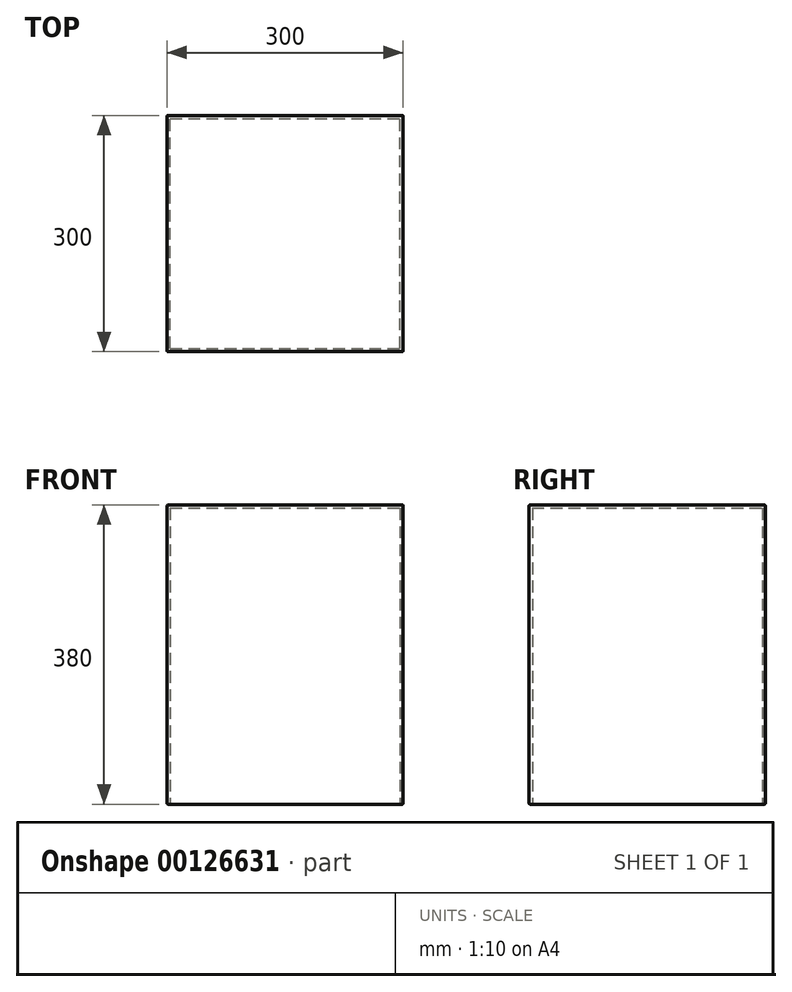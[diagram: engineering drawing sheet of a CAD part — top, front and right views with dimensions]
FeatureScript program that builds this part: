
annotation { "Feature Type Name" : "Feature", "Feature Type Description" : "" }
export const myFeature = defineFeature(function(context is Context, id is Id, definition is map)
    precondition{}
    {
        {
            var Q0;
            Q0=qCreatedBy(makeId("Front.planeOp"),FACE);
            var sketch = newSketch(context, id + "F0", { "sketchPlane" : qUnion([Q0])});
            skLineSegment(sketch, "E0.bottom", {"start": v(-252.56, 331.55) * mm, "end": v(47.44, 331.55) * mm});
            skLineSegment(sketch, "E0.top", {"start": v(-252.56, -48.45) * mm, "end": v(-248.56, -48.45) * mm});
            skLineSegment(sketch, "E0.left", {"start": v(-252.56, 331.55) * mm, "end": v(-252.56, -48.45) * mm});
            skLineSegment(sketch, "E0.right", {"start": v(47.44, 331.55) * mm, "end": v(47.44, -48.45) * mm});
            skLineSegment(sketch, "E1.1", {"start": v(-248.56, 327.55) * mm, "end": v(-248.56, -44.45) * mm});
            skLineSegment(sketch, "E1.2", {"start": v(-248.56, 327.55) * mm, "end": v(43.44, 327.55) * mm});
            skLineSegment(sketch, "E1.3", {"start": v(43.44, 327.55) * mm, "end": v(43.44, -44.45) * mm});
            skLineSegment(sketch, "E2", {"start": v(-248.56, -44.45) * mm, "end": v(-248.56, -48.45) * mm});
            skLineSegment(sketch, "E3", {"start": v(43.44, -44.45) * mm, "end": v(43.44, -48.45) * mm});
            skLineSegment(sketch, "E4.trimOffspring", {"start": v(43.44, -48.45) * mm, "end": v(47.44, -48.45) * mm});
            skSolve(sketch);
        }
        {
            var Q0;
            Q0=makeQuery(id+"F0.imprint","IMPRINT",FACE,{"disambiguationData":[TD([[makeQuery(id+"F0.imprint","IMPRINT",EDGE,{"derivedFrom":sQuery(id+"F0.wireOp",EDGE,"E0.bottom")}),-1.0]])]});
            extrude(context, id + "F1", {"entities" : qUnion([Q0]), "depth" : (300 - 8) * mm});
        }
        {
            var Q0;
            Q0=makeQuery(id+"F1.opExtrude","CAP_FACE",FACE,{"disambiguationData":[OSD([sQuery(id+"F0.wireOp",EDGE,"E0.bottom"),sQuery(id+"F0.wireOp",EDGE,"E0.top"),sQuery(id+"F0.wireOp",EDGE,"E0.left"),sQuery(id+"F0.wireOp",EDGE,"E0.right"),sQuery(id+"F0.wireOp",EDGE,"E1.1"),sQuery(id+"F0.wireOp",EDGE,"E1.2"),sQuery(id+"F0.wireOp",EDGE,"E1.3"),sQuery(id+"F0.wireOp",EDGE,"E2"),sQuery(id+"F0.wireOp",EDGE,"E3"),sQuery(id+"F0.wireOp",EDGE,"E4.trimOffspring")])],"isStart":false});
            var sketch = newSketch(context, id + "F2", { "sketchPlane" : qUnion([Q0])});
            skLineSegment(sketch, "E5.bottom", {"start": v(-252.56, 331.55) * mm, "end": v(47.44, 331.55) * mm});
            skLineSegment(sketch, "E5.top", {"start": v(-252.56, -48.45) * mm, "end": v(47.44, -48.45) * mm});
            skLineSegment(sketch, "E5.left", {"start": v(-252.56, 331.55) * mm, "end": v(-252.56, -48.45) * mm});
            skLineSegment(sketch, "E5.right", {"start": v(47.44, 331.55) * mm, "end": v(47.44, -48.45) * mm});
            skSolve(sketch);
        }
        {
            var Q0;
            Q0=makeQuery(id+"F2.imprint","IMPRINT",FACE,{"disambiguationData":[TD([[makeQuery(id+"F2.imprint","IMPRINT",EDGE,{"derivedFrom":makeQuery(id+"F1.opExtrude","CAP_EDGE",EDGE,{"disambiguationData":[OSD([sQuery(id+"F0.wireOp",EDGE,"E1.2")])],"isStart":false})}),-1.0]])]});
            var Q1;
            Q1=makeQuery(id+"F2.imprint","IMPRINT",FACE,{"disambiguationData":[TD([[makeQuery(id+"F2.imprint","IMPRINT",EDGE,{"derivedFrom":sQuery(id+"F2.wireOp",EDGE,"E5.bottom")}),-1.0]])]});
            extrude(context, id + "F3", {"entities" : qUnion([Q0, Q1]), "operationType" : NewBodyOperationType.ADD, "depth" : 4 * mm});
        }
        {
            var Q0;
            Q0=makeQuery(id+"F1.opExtrude","CAP_FACE",FACE,{"disambiguationData":[OSD([sQuery(id+"F0.wireOp",EDGE,"E0.bottom"),sQuery(id+"F0.wireOp",EDGE,"E0.top"),sQuery(id+"F0.wireOp",EDGE,"E0.left"),sQuery(id+"F0.wireOp",EDGE,"E0.right"),sQuery(id+"F0.wireOp",EDGE,"E1.1"),sQuery(id+"F0.wireOp",EDGE,"E1.2"),sQuery(id+"F0.wireOp",EDGE,"E1.3"),sQuery(id+"F0.wireOp",EDGE,"E2"),sQuery(id+"F0.wireOp",EDGE,"E3"),sQuery(id+"F0.wireOp",EDGE,"E4.trimOffspring")])],"isStart":true});
            var sketch = newSketch(context, id + "F4", { "sketchPlane" : qUnion([Q0])});
            skLineSegment(sketch, "E6.bottom", {"start": v(-47.44, 331.55) * mm, "end": v(252.56, 331.55) * mm});
            skLineSegment(sketch, "E6.top", {"start": v(-47.44, -48.45) * mm, "end": v(252.56, -48.45) * mm});
            skLineSegment(sketch, "E6.left", {"start": v(-47.44, 331.55) * mm, "end": v(-47.44, -48.45) * mm});
            skLineSegment(sketch, "E6.right", {"start": v(252.56, 331.55) * mm, "end": v(252.56, -48.45) * mm});
            skSolve(sketch);
        }
        {
            var Q0;
            Q0=makeQuery(id+"F4.imprint","IMPRINT",FACE,{"disambiguationData":[TD([[makeQuery(id+"F4.imprint","IMPRINT",EDGE,{"derivedFrom":sQuery(id+"F4.wireOp",EDGE,"E6.bottom")}),1.0]])]});
            var Q1;
            Q1=makeQuery(id+"F4.imprint","IMPRINT",FACE,{"disambiguationData":[TD([[makeQuery(id+"F4.imprint","IMPRINT",EDGE,{"derivedFrom":makeQuery(id+"F1.opExtrude","CAP_EDGE",EDGE,{"disambiguationData":[OSD([sQuery(id+"F0.wireOp",EDGE,"E1.2")])],"isStart":true})}),1.0]])]});
            extrude(context, id + "F5", {"entities" : qUnion([Q0, Q1]), "operationType" : NewBodyOperationType.ADD, "depth" : 4 * mm});
        }
        {
            var Q0;
            Q0=makeQuery(id+"F5.opExtrude","CAP_FACE",FACE,{"disambiguationData":[OSD([sQuery(id+"F4.wireOp",EDGE,"E6.bottom"),sQuery(id+"F4.wireOp",EDGE,"E6.top"),sQuery(id+"F4.wireOp",EDGE,"E6.left"),sQuery(id+"F4.wireOp",EDGE,"E6.right")])],"isStart":false});
            var Q1;
            Q1=makeQuery(id+"F5.boolean.opBoolean","MERGE",FACE,{"derivedFrom":[makeQuery(id+"F3.boolean.opBoolean","MERGE",FACE,{"derivedFrom":[makeQuery(id+"F1.opExtrude","SWEPT_FACE",FACE,{"disambiguationData":[OSD([sQuery(id+"F0.wireOp",EDGE,"E0.left")])]}),makeQuery(id+"F3.opExtrude","SWEPT_FACE",FACE,{"disambiguationData":[OSD([sQuery(id+"F2.wireOp",EDGE,"E5.left")])]})]}),makeQuery(id+"F5.opExtrude","SWEPT_FACE",FACE,{"disambiguationData":[OSD([sQuery(id+"F4.wireOp",EDGE,"E6.right")])]})]});
            var Q2;
            Q2=makeQuery(id+"F5.boolean.opBoolean","MERGE",FACE,{"derivedFrom":[makeQuery(id+"F3.boolean.opBoolean","MERGE",FACE,{"derivedFrom":[makeQuery(id+"F1.opExtrude","SWEPT_FACE",FACE,{"disambiguationData":[OSD([sQuery(id+"F0.wireOp",EDGE,"E0.bottom")])]}),makeQuery(id+"F3.opExtrude","SWEPT_FACE",FACE,{"disambiguationData":[OSD([sQuery(id+"F2.wireOp",EDGE,"E5.bottom")])]})]}),makeQuery(id+"F5.opExtrude","SWEPT_FACE",FACE,{"disambiguationData":[OSD([sQuery(id+"F4.wireOp",EDGE,"E6.bottom")])]})]});
            var Q3;
            Q3=makeQuery(id+"F3.opExtrude","CAP_FACE",FACE,{"disambiguationData":[OSD([sQuery(id+"F2.wireOp",EDGE,"E5.bottom"),sQuery(id+"F2.wireOp",EDGE,"E5.top"),sQuery(id+"F2.wireOp",EDGE,"E5.left"),sQuery(id+"F2.wireOp",EDGE,"E5.right")])],"isStart":false});
            var Q4;
            Q4=makeQuery(id+"F5.boolean.opBoolean","MERGE",FACE,{"derivedFrom":[makeQuery(id+"F3.boolean.opBoolean","MERGE",FACE,{"derivedFrom":[makeQuery(id+"F1.opExtrude","SWEPT_FACE",FACE,{"disambiguationData":[OSD([sQuery(id+"F0.wireOp",EDGE,"E0.right")])]}),makeQuery(id+"F3.opExtrude","SWEPT_FACE",FACE,{"disambiguationData":[OSD([sQuery(id+"F2.wireOp",EDGE,"E5.right")])]})]}),makeQuery(id+"F5.opExtrude","SWEPT_FACE",FACE,{"disambiguationData":[OSD([sQuery(id+"F4.wireOp",EDGE,"E6.left")])]})]});
            fillet(context, id + "F6", {"entities" : qUnion([Q0, Q1, Q2, Q3, Q4]), "radius" : 1 * mm, "tangentPropagation" : true, "allowEdgeOverflow" : false});
        }
    });
